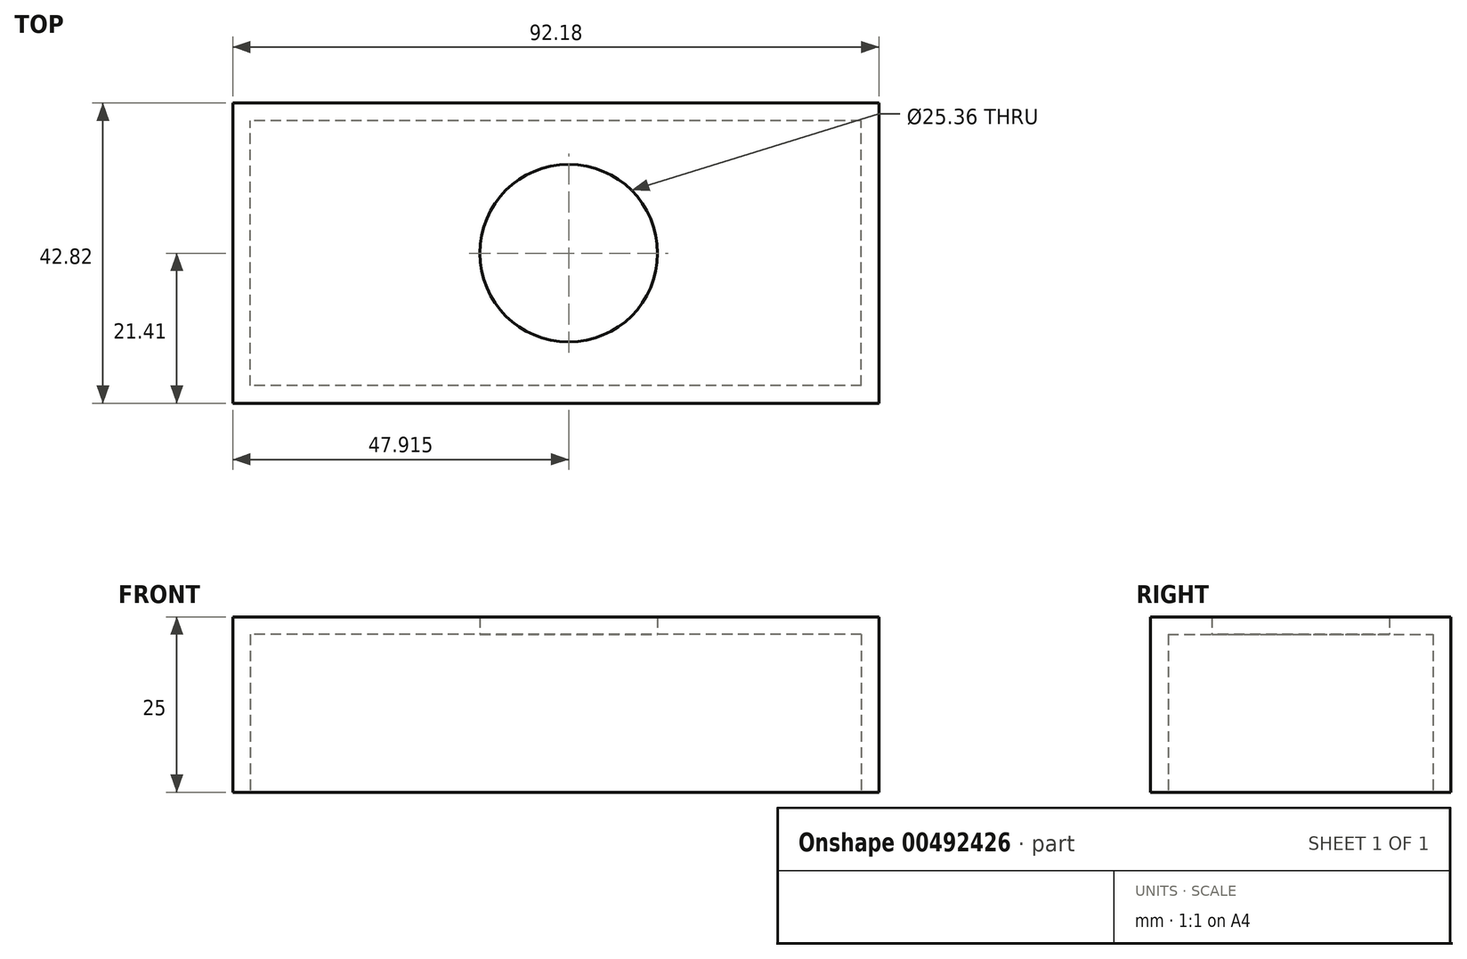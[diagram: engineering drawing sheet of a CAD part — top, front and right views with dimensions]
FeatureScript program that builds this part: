
annotation { "Feature Type Name" : "Feature", "Feature Type Description" : "" }
export const myFeature = defineFeature(function(context is Context, id is Id, definition is map)
    precondition{}
    {
        {
            var Q0;
            Q0=qCreatedBy(makeId("Top.planeOp"),FACE);
            var sketch = newSketch(context, id + "F0", { "sketchPlane" : qUnion([Q0])});
            skLineSegment(sketch, "E0.bottom", {"start": v(46.09, -21.41) * mm, "end": v(-46.09, -21.41) * mm});
            skLineSegment(sketch, "E0.top", {"start": v(46.09, 21.41) * mm, "end": v(-46.09, 21.41) * mm});
            skLineSegment(sketch, "E0.left", {"start": v(46.09, -21.41) * mm, "end": v(46.09, 21.41) * mm});
            skLineSegment(sketch, "E0.right", {"start": v(-46.09, -21.41) * mm, "end": v(-46.09, 21.41) * mm});
            skPoint(sketch, "E0.middle", {"position": v(0, 0) * mm});
            skSolve(sketch);
        }
        {
            var Q0;
            Q0=makeQuery(id+"F0.imprint","IMPRINT",FACE,{"disambiguationData":[TD([[makeQuery(id+"F0.imprint","IMPRINT",EDGE,{"derivedFrom":sQuery(id+"F0.wireOp",EDGE,"E0.bottom")}),-1.0]])]});
            extrude(context, id + "F1", {"entities" : qUnion([Q0]), "depth" : 25 * mm});
        }
        {
            var Q0;
            Q0=makeQuery(id+"F1.opExtrude","CAP_FACE",FACE,{"disambiguationData":[OSD([sQuery(id+"F0.wireOp",EDGE,"E0.bottom"),sQuery(id+"F0.wireOp",EDGE,"E0.top"),sQuery(id+"F0.wireOp",EDGE,"E0.left"),sQuery(id+"F0.wireOp",EDGE,"E0.right")])],"isStart":true});
            shell(context, id + "F2", {"entities" : qUnion([Q0]), "thickness" : 2.5 * mm});
        }
        {
            var Q0;
            Q0=makeQuery(id+"F2.opShell","OFFSET_FACE",FACE,{"disambiguationData":[OSD([sQuery(id+"F0.wireOp",EDGE,"E0.bottom"),sQuery(id+"F0.wireOp",EDGE,"E0.top"),sQuery(id+"F0.wireOp",EDGE,"E0.left"),sQuery(id+"F0.wireOp",EDGE,"E0.right")])]});
            var sketch = newSketch(context, id + "F3", { "sketchPlane" : qUnion([Q0])});
            skCircle(sketch, "E1", {"center": v(1.83, 0) * mm, "radius": 12.68 * mm});
            skSolve(sketch);
        }
        {
            var Q0;
            Q0=makeQuery(id+"F3.imprint","IMPRINT",FACE,{"disambiguationData":[TD([[makeQuery(id+"F3.imprint","IMPRINT",EDGE,{"derivedFrom":sQuery(id+"F3.wireOp",EDGE,"E1")}),1.0]])]});
            extrude(context, id + "F4", {"entities" : qUnion([Q0]), "operationType" : NewBodyOperationType.REMOVE, "oppositeDirection" : true, "depth" : 73.8 * mm});
        }
    });
